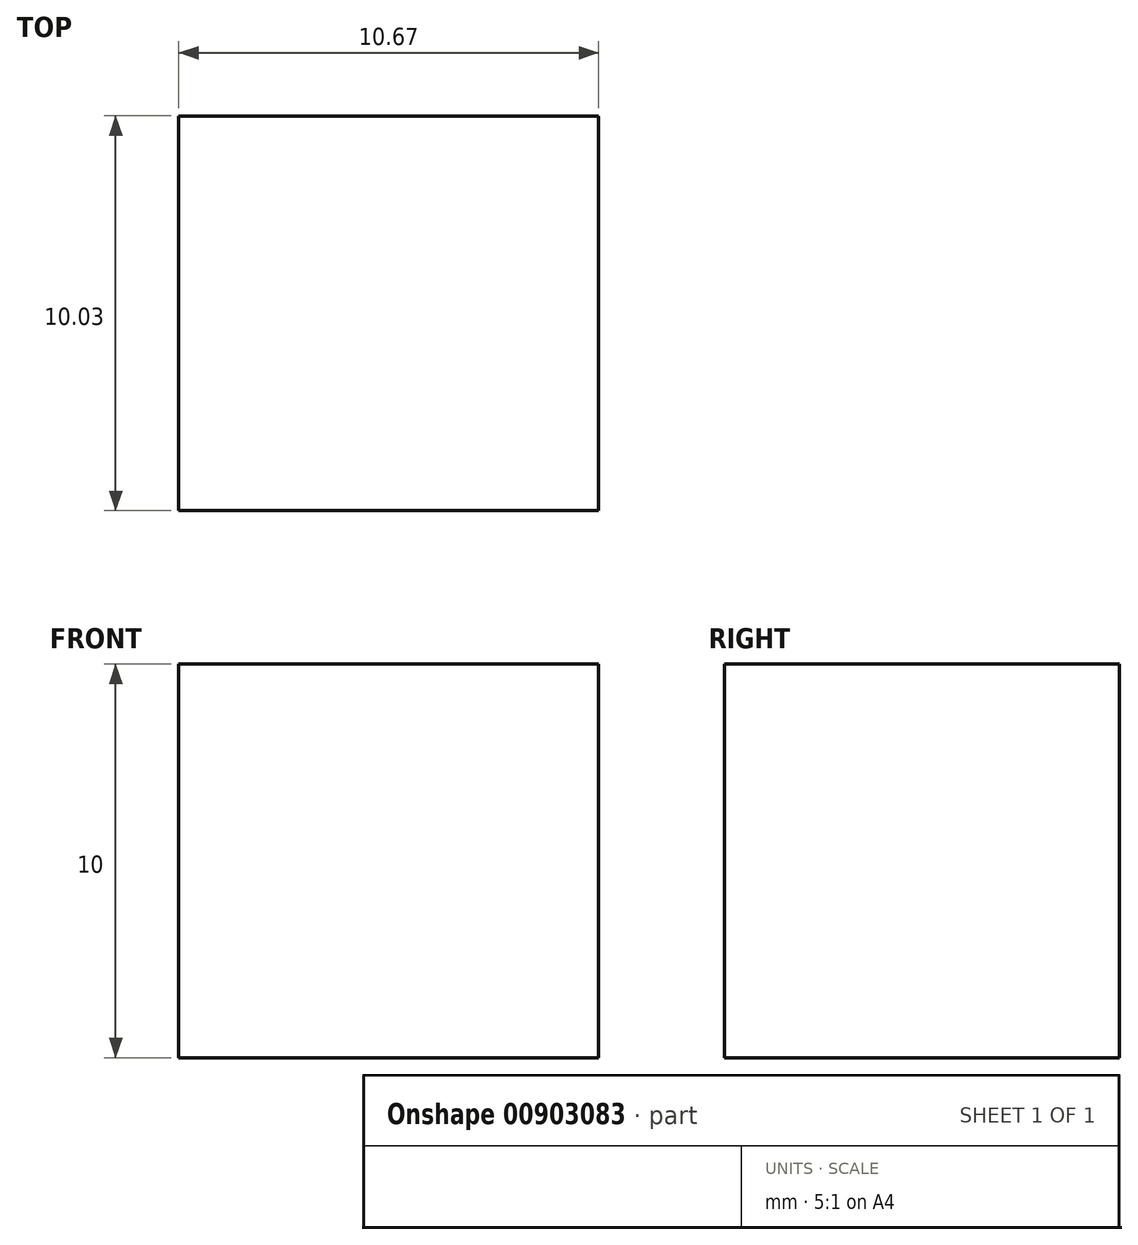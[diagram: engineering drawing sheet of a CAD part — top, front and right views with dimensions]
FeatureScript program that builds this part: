
annotation { "Feature Type Name" : "Feature", "Feature Type Description" : "" }
export const myFeature = defineFeature(function(context is Context, id is Id, definition is map)
    precondition{}
    {
        {
            var Q0;
            Q0=qCreatedBy(makeId("Top.planeOp"),FACE);
            var sketch = newSketch(context, id + "F0", { "sketchPlane" : qUnion([Q0])});
            skLineSegment(sketch, "E0.bottom", {"start": v(0.4, -0.41) * mm, "end": v(11.07, -0.41) * mm});
            skLineSegment(sketch, "E0.top", {"start": v(0.4, 9.62) * mm, "end": v(11.07, 9.62) * mm});
            skLineSegment(sketch, "E0.left", {"start": v(0.4, -0.41) * mm, "end": v(0.4, 9.62) * mm});
            skLineSegment(sketch, "E0.right", {"start": v(11.07, -0.41) * mm, "end": v(11.07, 9.62) * mm});
            skSolve(sketch);
        }
        {
            var Q0;
            Q0 = qSketchRegion(id + "F0", true);
            extrude(context, id + "F1", {"entities" : qUnion([Q0]), "depth" : 10 * mm, "offsetDistance" : 25 * mm});
        }
    });
